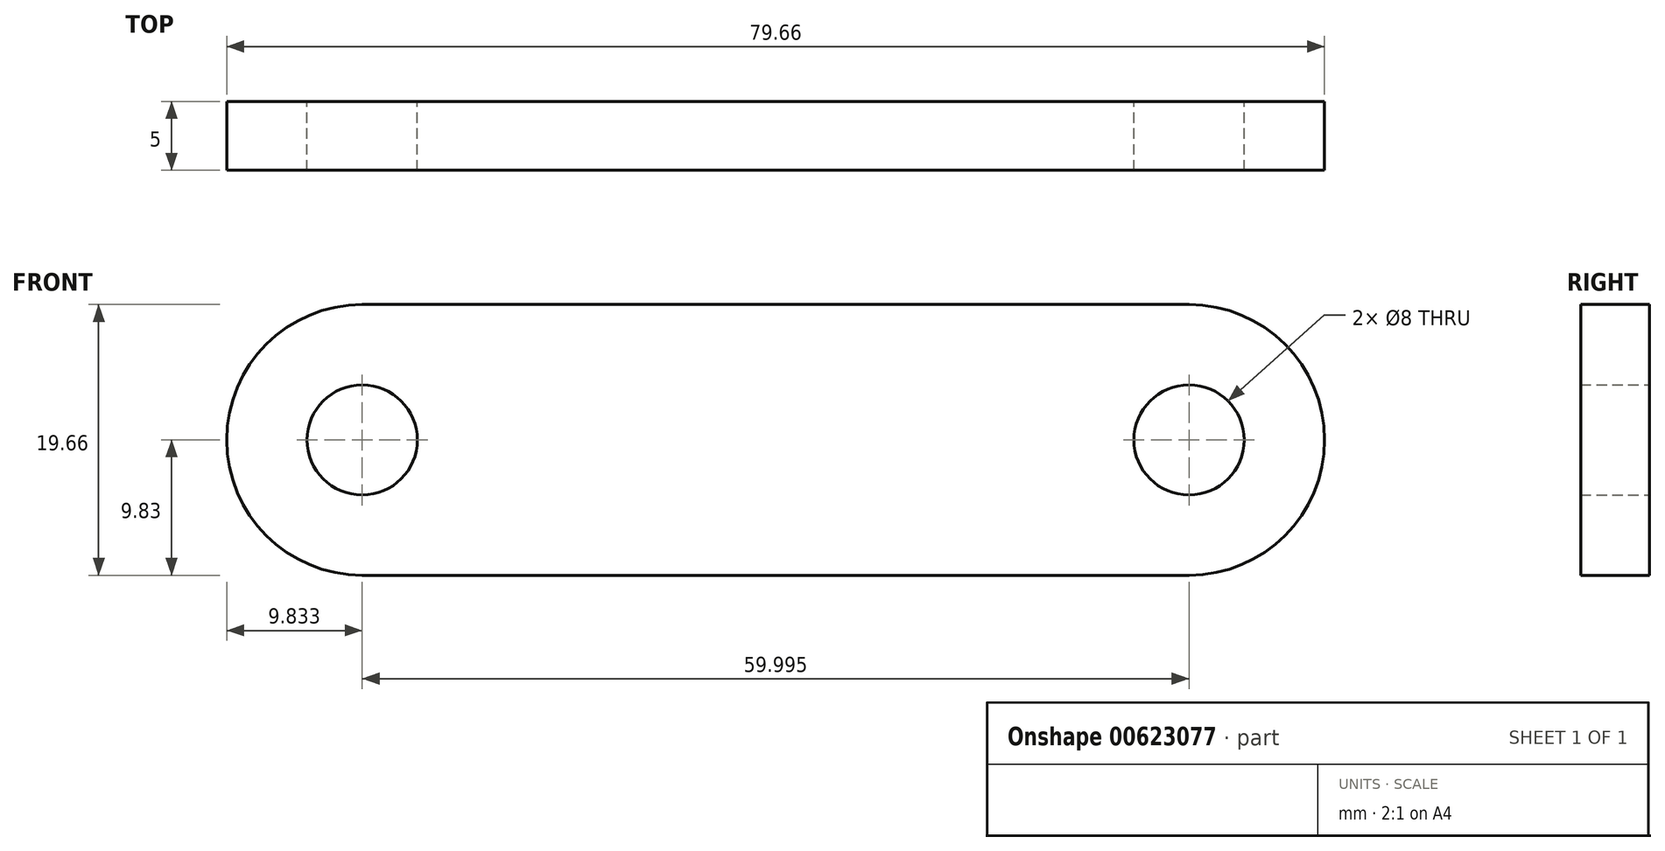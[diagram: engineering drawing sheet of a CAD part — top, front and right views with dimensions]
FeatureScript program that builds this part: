
annotation { "Feature Type Name" : "Feature", "Feature Type Description" : "" }
export const myFeature = defineFeature(function(context is Context, id is Id, definition is map)
    precondition{}
    {
        {
            var Q0;
            Q0=qCreatedBy(makeId("Front.planeOp"),FACE);
            var sketch = newSketch(context, id + "F0", { "sketchPlane" : qUnion([Q0])});
            skLineSegment(sketch, "E0", {"start": v(0, 0) * mm, "end": v(-30, 0) * mm});
            skLineSegment(sketch, "E1", {"start": v(0, 0) * mm, "end": v(0, 19.1) * mm});
            skArc(sketch, "E2", {"start": v(-30, 9.83) * mm, "mid": v(-39.83, 0) * mm, "end": v(-30, -9.83) * mm});
            skCircle(sketch, "E3", {"center": v(-30, 0) * mm, "radius": 4 * mm});
            skLineSegment(sketch, "E4.0", {"start": v(0, 9.83) * mm, "end": v(-30, 9.83) * mm});
            skLineSegment(sketch, "E5.0", {"start": v(0, -9.83) * mm, "end": v(-30, -9.83) * mm});
            skLineSegment(sketch, "E6.MirrorCS", {"start": v(0, 0) * mm, "end": v(30, 0) * mm});
            skArc(sketch, "E7.MirrorCS", {"start": v(30, 9.83) * mm, "mid": v(39.83, 0) * mm, "end": v(30, -9.83) * mm});
            skLineSegment(sketch, "E8.MirrorCS", {"start": v(0, -9.83) * mm, "end": v(30, -9.83) * mm});
            skLineSegment(sketch, "E9.MirrorCS", {"start": v(0, 9.83) * mm, "end": v(30, 9.83) * mm});
            skCircle(sketch, "E10.MirrorC", {"center": v(30, 0) * mm, "radius": 4 * mm});
            skSolve(sketch);
        }
        {
            var Q0;
            Q0=makeQuery(id+"F0.imprint","IMPRINT",FACE,{"disambiguationData":[TD([[makeQuery(id+"F0.imprint","IMPRINT",EDGE,{"derivedFrom":sQuery(id+"F0.wireOp",EDGE,"E2")}),1.0]])]});
            extrude(context, id + "F1", {"entities" : qUnion([Q0]), "endBound" : BoundingType.SYMMETRIC, "depth" : 5 * mm, "offsetDistance" : 25.4 * mm});
        }
    });
